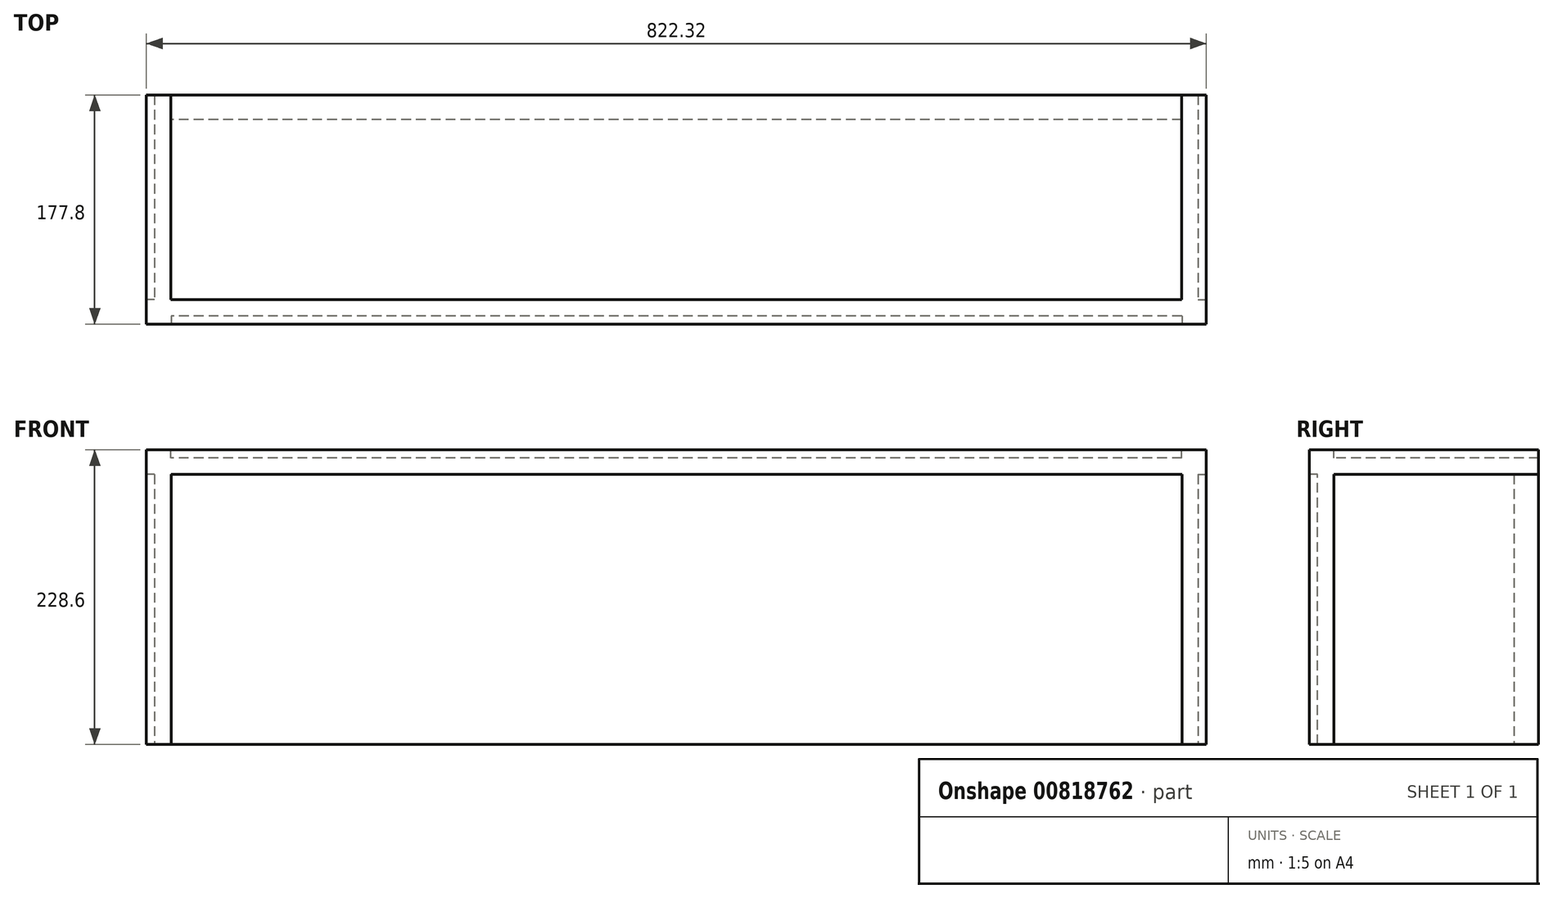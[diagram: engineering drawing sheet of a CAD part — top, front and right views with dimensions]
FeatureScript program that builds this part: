
annotation { "Feature Type Name" : "Feature", "Feature Type Description" : "" }
export const myFeature = defineFeature(function(context is Context, id is Id, definition is map)
    precondition{}
    {
        {
            var Q0;
            Q0=qCreatedBy(makeId("Top.planeOp"),FACE);
            var sketch = newSketch(context, id + "F0", { "sketchPlane" : qUnion([Q0])});
            skLineSegment(sketch, "E0.bottom", {"start": v(411.16, 88.9) * mm, "end": v(-411.16, 88.9) * mm});
            skLineSegment(sketch, "E0.top", {"start": v(411.16, -88.9) * mm, "end": v(-411.16, -88.9) * mm});
            skLineSegment(sketch, "E0.left", {"start": v(411.16, 88.9) * mm, "end": v(411.16, -88.9) * mm});
            skLineSegment(sketch, "E0.right", {"start": v(-411.16, 88.9) * mm, "end": v(-411.16, -88.9) * mm});
            skPoint(sketch, "E0.middle", {"position": v(0, 0) * mm});
            skSolve(sketch);
        }
        {
            var Q0;
            Q0=makeQuery(id+"F0.imprint","IMPRINT",FACE,{"disambiguationData":[TD([[makeQuery(id+"F0.imprint","IMPRINT",EDGE,{"derivedFrom":sQuery(id+"F0.wireOp",EDGE,"E0.bottom")}),1.0]])]});
            extrude(context, id + "F1", {"entities" : qUnion([Q0]), "depth" : 228.6 * mm, "offsetDistance" : 25.4 * mm});
        }
        {
            var Q0;
            Q0=makeQuery(id+"F1.opExtrude","CAP_FACE",FACE,{"disambiguationData":[OSD([sQuery(id+"F0.wireOp",EDGE,"E0.bottom"),sQuery(id+"F0.wireOp",EDGE,"E0.top"),sQuery(id+"F0.wireOp",EDGE,"E0.left"),sQuery(id+"F0.wireOp",EDGE,"E0.right")])],"isStart":true});
            shell(context, id + "F2", {"entities" : qUnion([Q0]), "thickness" : 19.05 * mm});
        }
        {
            var Q0;
            Q0=makeQuery(id+"F1.opExtrude","SWEPT_FACE",FACE,{"disambiguationData":[OSD([sQuery(id+"F0.wireOp",EDGE,"E0.top")])]});
            var sketch = newSketch(context, id + "F3", { "sketchPlane" : qUnion([Q0])});
            skLineSegment(sketch, "E1.bottom", {"start": v(-391.97, 0) * mm, "end": v(392.26, 0) * mm});
            skLineSegment(sketch, "E1.top", {"start": v(-391.97, 209.55) * mm, "end": v(392.26, 209.55) * mm});
            skLineSegment(sketch, "E1.left", {"start": v(-391.97, 0) * mm, "end": v(-391.97, 209.55) * mm});
            skLineSegment(sketch, "E1.right", {"start": v(392.26, 0) * mm, "end": v(392.26, 209.55) * mm});
            skSolve(sketch);
        }
        {
            var Q0;
            Q0=makeQuery(id+"F3.imprint","IMPRINT",FACE,{"disambiguationData":[TD([[makeQuery(id+"F3.imprint","IMPRINT",EDGE,{"derivedFrom":sQuery(id+"F3.wireOp",EDGE,"E1.bottom")}),-1.0]])]});
            extrude(context, id + "F4", {"entities" : qUnion([Q0]), "operationType" : NewBodyOperationType.REMOVE, "oppositeDirection" : true, "depth" : 6.35 * mm, "offsetDistance" : 25.4 * mm});
        }
        {
            var Q0;
            Q0=makeQuery(id+"F1.opExtrude","SWEPT_FACE",FACE,{"disambiguationData":[OSD([sQuery(id+"F0.wireOp",EDGE,"E0.right")])]});
            var sketch = newSketch(context, id + "F5", { "sketchPlane" : qUnion([Q0])});
            skLineSegment(sketch, "E2.bottom", {"start": v(-88.9, 0) * mm, "end": v(69.85, 0) * mm});
            skLineSegment(sketch, "E2.top", {"start": v(-88.9, 209.55) * mm, "end": v(69.85, 209.55) * mm});
            skLineSegment(sketch, "E2.left", {"start": v(-88.9, 0) * mm, "end": v(-88.9, 209.55) * mm});
            skLineSegment(sketch, "E2.right", {"start": v(69.85, 0) * mm, "end": v(69.85, 209.55) * mm});
            skSolve(sketch);
        }
        {
            var Q0;
            Q0=makeQuery(id+"F5.imprint","IMPRINT",FACE,{"disambiguationData":[TD([[makeQuery(id+"F5.imprint","IMPRINT",EDGE,{"derivedFrom":sQuery(id+"F5.wireOp",EDGE,"E2.bottom")}),1.0]])]});
            extrude(context, id + "F6", {"entities" : qUnion([Q0]), "operationType" : NewBodyOperationType.REMOVE, "oppositeDirection" : true, "depth" : 6.35 * mm, "offsetDistance" : 25.4 * mm});
        }
        {
            var Q0;
            Q0=makeQuery(id+"F1.opExtrude","SWEPT_FACE",FACE,{"disambiguationData":[OSD([sQuery(id+"F0.wireOp",EDGE,"E0.left")])]});
            var sketch = newSketch(context, id + "F7", { "sketchPlane" : qUnion([Q0])});
            skLineSegment(sketch, "E3.bottom", {"start": v(88.9, 0) * mm, "end": v(-69.85, 0) * mm});
            skLineSegment(sketch, "E3.top", {"start": v(88.9, 209.55) * mm, "end": v(-69.85, 209.55) * mm});
            skLineSegment(sketch, "E3.left", {"start": v(88.9, 0) * mm, "end": v(88.9, 209.55) * mm});
            skLineSegment(sketch, "E3.right", {"start": v(-69.85, 0) * mm, "end": v(-69.85, 209.55) * mm});
            skSolve(sketch);
        }
        {
            var Q0;
            Q0=makeQuery(id+"F7.imprint","IMPRINT",FACE,{"disambiguationData":[TD([[makeQuery(id+"F7.imprint","IMPRINT",EDGE,{"derivedFrom":sQuery(id+"F7.wireOp",EDGE,"E3.bottom")}),-1.0]])]});
            extrude(context, id + "F8", {"entities" : qUnion([Q0]), "operationType" : NewBodyOperationType.REMOVE, "oppositeDirection" : true, "depth" : 6.35 * mm, "offsetDistance" : 25.4 * mm});
        }
        {
            var Q0;
            Q0=makeQuery(id+"F1.opExtrude","CAP_FACE",FACE,{"disambiguationData":[OSD([sQuery(id+"F0.wireOp",EDGE,"E0.bottom"),sQuery(id+"F0.wireOp",EDGE,"E0.top"),sQuery(id+"F0.wireOp",EDGE,"E0.left"),sQuery(id+"F0.wireOp",EDGE,"E0.right")])],"isStart":false});
            var sketch = newSketch(context, id + "F9", { "sketchPlane" : qUnion([Q0])});
            skLineSegment(sketch, "E4", {"start": v(411.16, 88.9) * mm, "end": v(392.11, 88.9) * mm});
            skLineSegment(sketch, "E5.bottom", {"start": v(392.11, 88.9) * mm, "end": v(-392.11, 88.9) * mm});
            skLineSegment(sketch, "E5.top", {"start": v(392.11, -69.85) * mm, "end": v(-392.11, -69.85) * mm});
            skLineSegment(sketch, "E5.left", {"start": v(392.11, 88.9) * mm, "end": v(392.11, -69.85) * mm});
            skLineSegment(sketch, "E5.right", {"start": v(-392.11, 88.9) * mm, "end": v(-392.11, -69.85) * mm});
            skSolve(sketch);
        }
        {
            var Q0;
            Q0=makeQuery(id+"F9.imprint","IMPRINT",FACE,{"disambiguationData":[TD([[makeQuery(id+"F9.imprint","IMPRINT",EDGE,{"derivedFrom":sQuery(id+"F9.wireOp",EDGE,"E5.bottom")}),1.0]])]});
            extrude(context, id + "F10", {"entities" : qUnion([Q0]), "operationType" : NewBodyOperationType.REMOVE, "oppositeDirection" : true, "depth" : 6.35 * mm, "offsetDistance" : 25.4 * mm});
        }
    });
